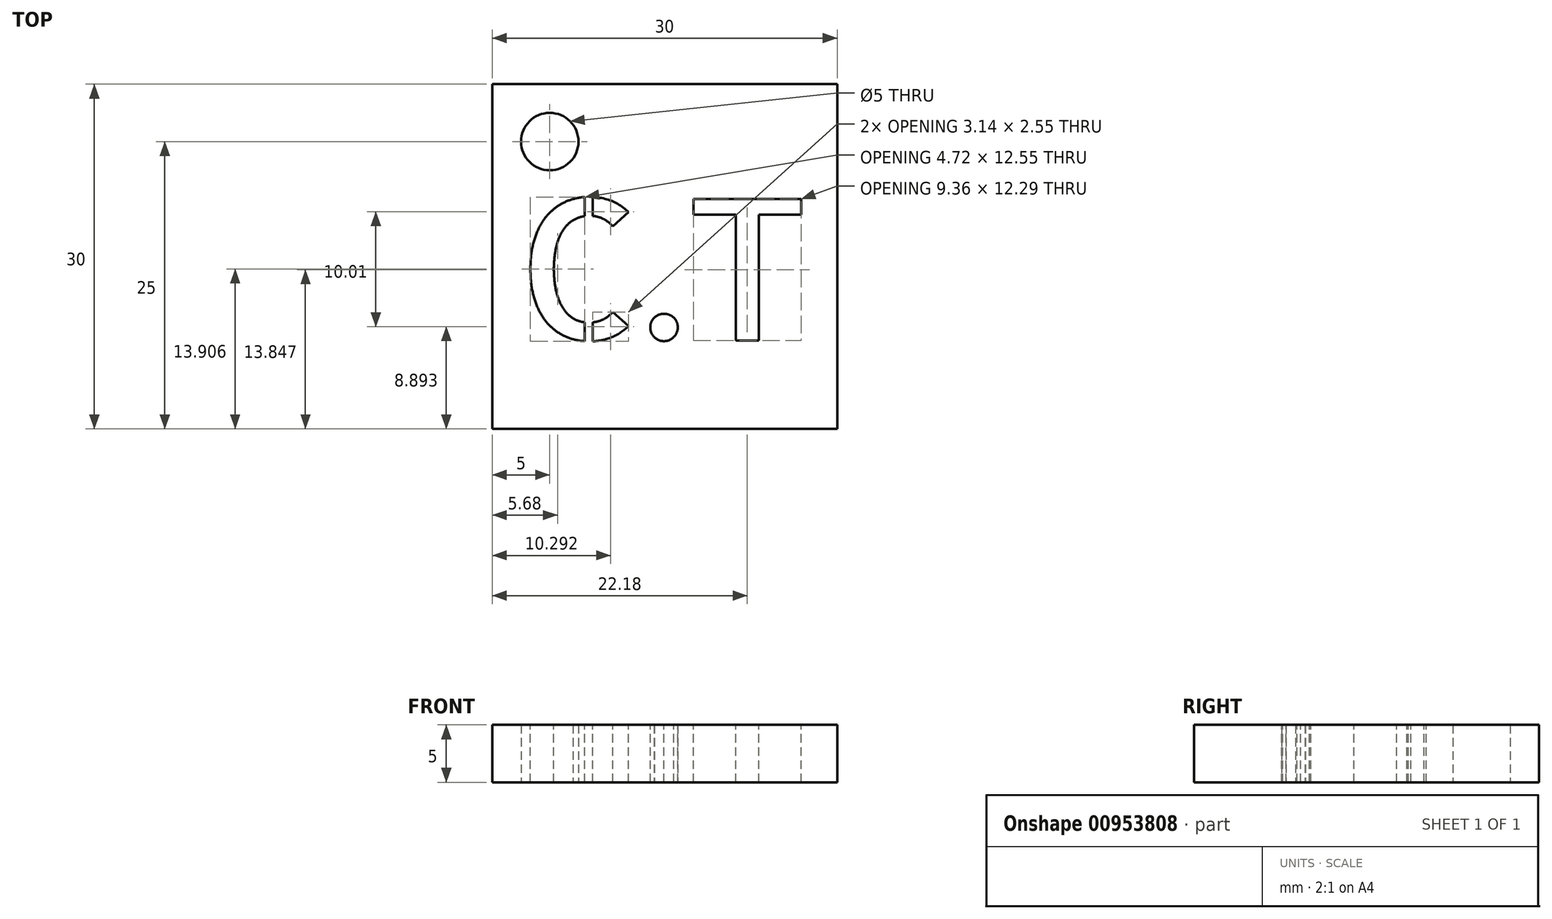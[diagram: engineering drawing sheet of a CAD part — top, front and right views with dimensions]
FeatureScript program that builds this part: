
annotation { "Feature Type Name" : "Feature", "Feature Type Description" : "" }
export const myFeature = defineFeature(function(context is Context, id is Id, definition is map)
    precondition{}
    {
        {
            var Q0;
            Q0=qCreatedBy(makeId("Top.planeOp"),FACE);
            var sketch = newSketch(context, id + "F0", { "sketchPlane" : qUnion([Q0])});
            skLineSegment(sketch, "E0.bottom", {"start": v(0, 0) * mm, "end": v(-30, 0) * mm});
            skLineSegment(sketch, "E0.top", {"start": v(0, 30) * mm, "end": v(-30, 30) * mm});
            skLineSegment(sketch, "E0.left", {"start": v(0, 0) * mm, "end": v(0, 30) * mm});
            skLineSegment(sketch, "E0.right", {"start": v(-30, 0) * mm, "end": v(-30, 30) * mm});
            skCircle(sketch, "E1", {"center": v(-25, 25) * mm, "radius": 2.5 * mm});
            skSolve(sketch);
        }
        {
            var Q0;
            Q0=makeQuery(id+"F0.imprint","IMPRINT",FACE,{"disambiguationData":[TD([[makeQuery(id+"F0.imprint","IMPRINT",EDGE,{"derivedFrom":sQuery(id+"F0.wireOp",EDGE,"E0.bottom")}),-1.0]])]});
            extrude(context, id + "F1", {"entities" : qUnion([Q0]), "depth" : 5 * mm, "offsetDistance" : 25 * mm});
        }
        {
            var Q0;
            Q0=makeQuery(id+"F1.opExtrude","CAP_FACE",FACE,{"disambiguationData":[OSD([sQuery(id+"F0.wireOp",EDGE,"E0.bottom"),sQuery(id+"F0.wireOp",EDGE,"E0.top"),sQuery(id+"F0.wireOp",EDGE,"E0.left"),sQuery(id+"F0.wireOp",EDGE,"E0.right"),sQuery(id+"F0.wireOp",EDGE,"E1")])],"isStart":false});
            var sketch = newSketch(context, id + "F2", { "sketchPlane" : qUnion([Q0])});
            skText(sketch, "E2", { "text": "C.T", "fontName": "AllertaStencil-Regular.ttf"});
            const initialGuessF2  = {"E2": [-0.028, 0.0077, 1, 0, 0.0123]};
            skSetInitialGuess(sketch, initialGuessF2);
            skSolve(sketch);
        }
        {
            var Q0;
            Q0 = qSketchRegion(id + "F2", true);
            extrude(context, id + "F3", {"entities" : qUnion([Q0]), "operationType" : NewBodyOperationType.REMOVE, "endBound" : BoundingType.THROUGH_ALL, "oppositeDirection" : true, "depth" : 25 * mm, "offsetDistance" : 25 * mm});
        }
    });
